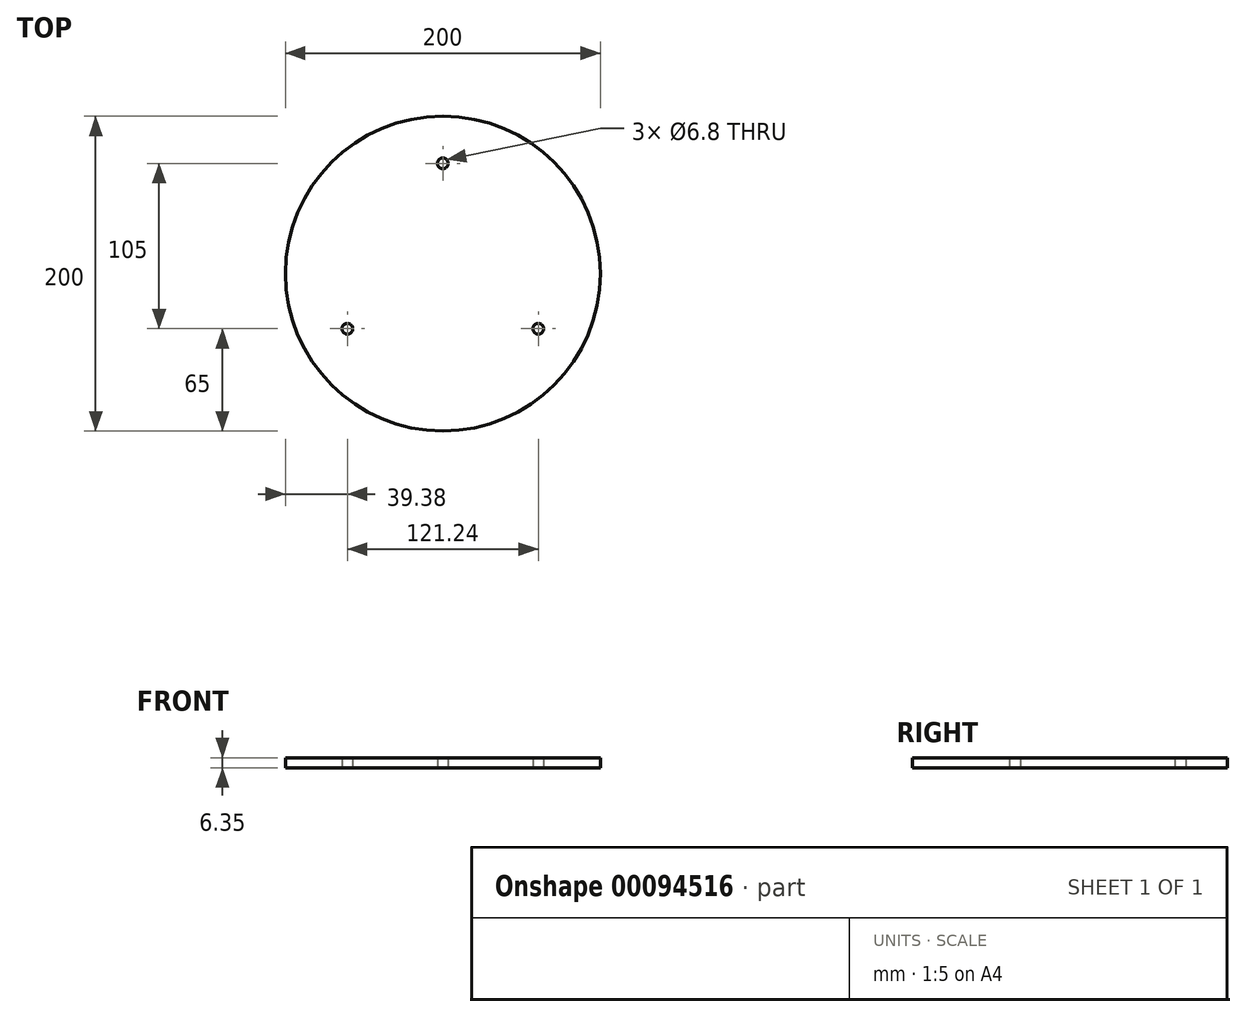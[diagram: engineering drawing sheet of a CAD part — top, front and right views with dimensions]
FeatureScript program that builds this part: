
annotation { "Feature Type Name" : "Feature", "Feature Type Description" : "" }
export const myFeature = defineFeature(function(context is Context, id is Id, definition is map)
    precondition{}
    {
        {
            var Q0;
            Q0=qCreatedBy(makeId("Top.planeOp"),FACE);
            var sketch = newSketch(context, id + "F0", { "sketchPlane" : qUnion([Q0])});
            skCircle(sketch, "E0", {"center": v(0, 0) * mm, "radius": 100 * mm});
            skPoint(sketch, "E1", {"position": v(0, 70) * mm});
            skPoint(sketch, "E2", {"position": v(60.62, -35) * mm});
            skPoint(sketch, "E3", {"position": v(-60.62, -35) * mm});
            skSolve(sketch);
        }
        {
            var Q0;
            Q0=makeQuery(id+"F0.imprint","IMPRINT",FACE,{"disambiguationData":[TD([[makeQuery(id+"F0.imprint","IMPRINT",EDGE,{"derivedFrom":sQuery(id+"F0.wireOp",EDGE,"E0")}),1.0]])]});
            extrude(context, id + "F1", {"entities" : qUnion([Q0]), "depth" : 6.35 * mm});
        }
        {
            var Q0;
            Q0=sQuery(id+"F0.wireOp",VERTEX,"E2");
            var Q1;
            Q1=sQuery(id+"F0.wireOp",VERTEX,"E1");
            var Q2;
            Q2=sQuery(id+"F0.wireOp",VERTEX,"E3");
            var Q3;
            Q3=makeQuery(id+"F1.opExtrude","SWEPT_BODY",BODY,{"disambiguationData":[OSD([sQuery(id+"F0.wireOp",EDGE,"E0")])]});
            hole(context, id + "F2", {"style" : HoleStyle.SIMPLE, "endStyle" : HoleEndStyle.THROUGH, "oppositeDirection" : true, "standardTappedOrClearance" : lookupTablePath({ "standard" : "ISO", "engagement" : "75%", "pitch" : "1.25 mm", "size" : "M8", "type" : "Tapped" }), "standardBlindInLast" : lookupTablePath({ "standard" : "ISO", "engagement" : "75%", "pitch" : "1.25 mm", "size" : "M8", "type" : "Tapped" }), "holeDiameter" : 6.8 * mm, "locations" : qUnion([Q0, Q1, Q2]), "scope" : qUnion([Q3]), "isTappedThrough" : true, "majorDiameter" : 8 * mm, "showTappedDepth" : true});
        }
    });
